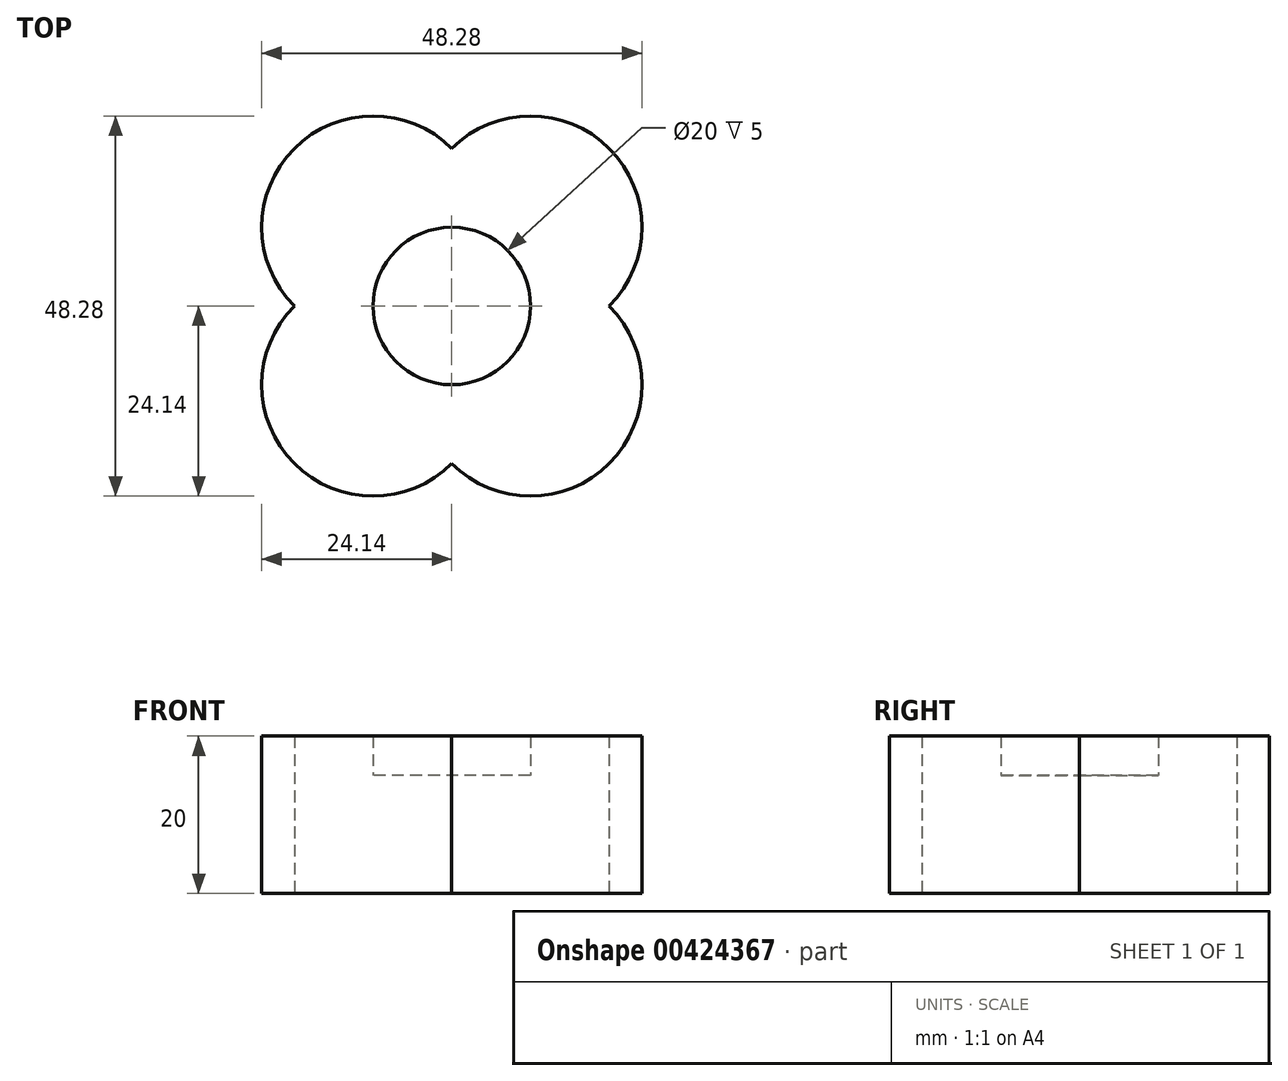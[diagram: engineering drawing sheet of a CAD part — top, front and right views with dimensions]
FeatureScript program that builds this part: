
annotation { "Feature Type Name" : "Feature", "Feature Type Description" : "" }
export const myFeature = defineFeature(function(context is Context, id is Id, definition is map)
    precondition{}
    {
        {
            var Q0;
            Q0=qCreatedBy(makeId("Top.planeOp"),FACE);
            var sketch = newSketch(context, id + "F0", { "sketchPlane" : qUnion([Q0])});
            skPoint(sketch, "E0.middle", {"position": v(0, 0) * mm});
            skPoint(sketch, "E1", {"position": v(10, 10) * mm});
            skCircle(sketch, "E2", {"center": v(10, 10) * mm, "radius": 14.14 * mm});
            skCircle(sketch, "E3", {"center": v(10, -10) * mm, "radius": 14.14 * mm});
            skCircle(sketch, "E4", {"center": v(-10, -10) * mm, "radius": 14.14 * mm});
            skCircle(sketch, "E5", {"center": v(-10, 10) * mm, "radius": 14.14 * mm});
            skSolve(sketch);
        }
        {
            var Q0;
            {var subQ0=sQuery(id+"F0.wireOp",EDGE,"E5");var subQ1=sQuery(id+"F0.wireOp",EDGE,"E2");var subQ2=makeQuery(id+"F0.imprint","INTERSECT",VERTEX,{"derivedFrom":[subQ1,subQ0]});Q0=makeQuery(id+"F0.imprint","IMPRINT",FACE,{"disambiguationData":[TD([[makeQuery(id+"F0.imprint","IMPRINT",EDGE,{"disambiguationData":[TD([[subQ2,-1.0]])],"derivedFrom":subQ0}),1.0]])]});}
            var Q1;
            {var subQ0=sQuery(id+"F0.wireOp",EDGE,"E5");var subQ1=sQuery(id+"F0.wireOp",EDGE,"E2");var subQ2=makeQuery(id+"F0.imprint","INTERSECT",VERTEX,{"derivedFrom":[subQ1,subQ0]});Q1=makeQuery(id+"F0.imprint","IMPRINT",FACE,{"disambiguationData":[TD([[makeQuery(id+"F0.imprint","IMPRINT",EDGE,{"disambiguationData":[TD([[subQ2,1.0]])],"derivedFrom":subQ1}),1.0]])]});}
            var Q2;
            {var subQ0=sQuery(id+"F0.wireOp",EDGE,"E5");var subQ1=sQuery(id+"F0.wireOp",EDGE,"E2");var subQ2=makeQuery(id+"F0.imprint","INTERSECT",VERTEX,{"derivedFrom":[subQ1,subQ0]});Q2=makeQuery(id+"F0.imprint","IMPRINT",FACE,{"disambiguationData":[TD([[makeQuery(id+"F0.imprint","IMPRINT",EDGE,{"disambiguationData":[TD([[subQ2,-1.0]])],"derivedFrom":subQ1}),1.0]])]});}
            var Q3;
            {var subQ0=sQuery(id+"F0.wireOp",EDGE,"E5");var subQ1=sQuery(id+"F0.wireOp",EDGE,"E4");var subQ2=makeQuery(id+"F0.imprint","INTERSECT",VERTEX,{"derivedFrom":[subQ1,subQ0]});Q3=makeQuery(id+"F0.imprint","IMPRINT",FACE,{"disambiguationData":[TD([[makeQuery(id+"F0.imprint","IMPRINT",EDGE,{"disambiguationData":[TD([[subQ2,1.0]])],"derivedFrom":subQ1}),1.0]])]});}
            var Q4;
            {var subQ0=sQuery(id+"F0.wireOp",EDGE,"E4");var subQ1=sQuery(id+"F0.wireOp",EDGE,"E3");var subQ2=makeQuery(id+"F0.imprint","INTERSECT",VERTEX,{"derivedFrom":[subQ1,subQ0]});Q4=makeQuery(id+"F0.imprint","IMPRINT",FACE,{"disambiguationData":[TD([[makeQuery(id+"F0.imprint","IMPRINT",EDGE,{"disambiguationData":[TD([[subQ2,1.0]])],"derivedFrom":subQ1}),1.0]])]});}
            var Q5;
            {var subQ0=sQuery(id+"F0.wireOp",EDGE,"E3");var subQ1=sQuery(id+"F0.wireOp",EDGE,"E2");var subQ2=makeQuery(id+"F0.imprint","INTERSECT",VERTEX,{"derivedFrom":[subQ1,subQ0]});Q5=makeQuery(id+"F0.imprint","IMPRINT",FACE,{"disambiguationData":[TD([[makeQuery(id+"F0.imprint","IMPRINT",EDGE,{"disambiguationData":[TD([[subQ2,1.0]])],"derivedFrom":subQ1}),1.0]])]});}
            var Q6;
            {var subQ0=sQuery(id+"F0.wireOp",EDGE,"E3");var subQ1=sQuery(id+"F0.wireOp",EDGE,"E2");var subQ2=makeQuery(id+"F0.imprint","INTERSECT",VERTEX,{"derivedFrom":[subQ1,subQ0]});Q6=makeQuery(id+"F0.imprint","IMPRINT",FACE,{"disambiguationData":[TD([[makeQuery(id+"F0.imprint","IMPRINT",EDGE,{"disambiguationData":[TD([[subQ2,1.0]])],"derivedFrom":subQ0}),1.0]])]});}
            var Q7;
            {var subQ0=sQuery(id+"F0.wireOp",EDGE,"E4");var subQ1=sQuery(id+"F0.wireOp",EDGE,"E3");var subQ2=makeQuery(id+"F0.imprint","INTERSECT",VERTEX,{"derivedFrom":[subQ1,subQ0]});Q7=makeQuery(id+"F0.imprint","IMPRINT",FACE,{"disambiguationData":[TD([[makeQuery(id+"F0.imprint","IMPRINT",EDGE,{"disambiguationData":[TD([[subQ2,1.0]])],"derivedFrom":subQ0}),1.0]])]});}
            extrude(context, id + "F1", {"entities" : qUnion([Q0, Q1, Q2, Q3, Q4, Q5, Q6, Q7]), "depth" : 15 * mm, "offsetDistance" : 25 * mm});
        }
        {
            var Q0;
            Q0=makeQuery(id+"F1.opExtrude","CAP_FACE",FACE,{"disambiguationData":[OSD([sQuery(id+"F0.wireOp",EDGE,"E2"),sQuery(id+"F0.wireOp",EDGE,"E3"),sQuery(id+"F0.wireOp",EDGE,"E4"),sQuery(id+"F0.wireOp",EDGE,"E5")])],"isStart":false});
            var sketch = newSketch(context, id + "F2", { "sketchPlane" : qUnion([Q0])});
            skCircle(sketch, "E6", {"center": v(0, 0) * mm, "radius": 10 * mm});
            skLineSegment(sketch, "E7", {"start": v(0, 0) * mm, "end": v(10, 0) * mm});
            skSolve(sketch);
        }
        {
            var Q0;
            Q0=makeQuery(id+"F2.imprint","IMPRINT",FACE,{"disambiguationData":[TD([[makeQuery(id+"F2.imprint","IMPRINT",EDGE,{"derivedFrom":sQuery(id+"F2.wireOp",EDGE,"E6")}),-1.0]])]});
            extrude(context, id + "F3", {"entities" : qUnion([Q0]), "operationType" : NewBodyOperationType.ADD, "depth" : 5 * mm, "offsetDistance" : 25 * mm});
        }
    });
